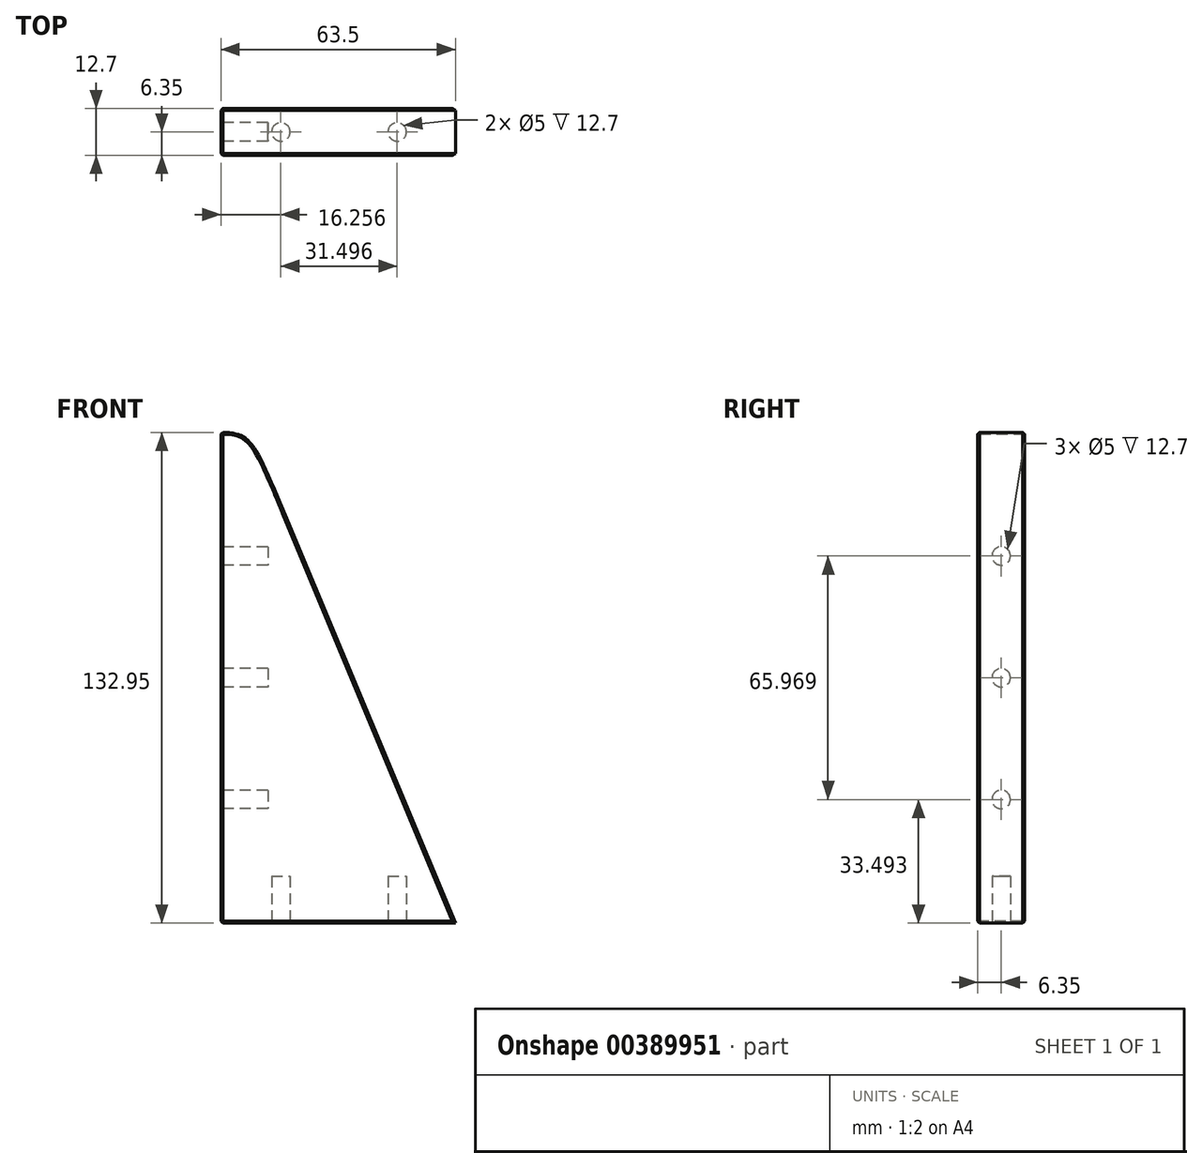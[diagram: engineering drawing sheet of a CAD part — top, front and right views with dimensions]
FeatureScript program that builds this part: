
annotation { "Feature Type Name" : "Feature", "Feature Type Description" : "" }
export const myFeature = defineFeature(function(context is Context, id is Id, definition is map)
    precondition{}
    {
        {
            var Q0;
            Q0=qCreatedBy(makeId("Front.planeOp"),FACE);
            var sketch = newSketch(context, id + "F0", { "sketchPlane" : qUnion([Q0])});
            skLineSegment(sketch, "E0.bottom", {"start": v(63.5, 76.2) * mm, "end": v(-63.5, 76.2) * mm});
            skLineSegment(sketch, "E0.top", {"start": v(63.5, -76.2) * mm, "end": v(-63.5, -76.2) * mm});
            skLineSegment(sketch, "E0.left", {"start": v(63.5, 76.2) * mm, "end": v(63.5, -76.2) * mm});
            skLineSegment(sketch, "E0.right", {"start": v(-63.5, 76.2) * mm, "end": v(-63.5, -76.2) * mm});
            skPoint(sketch, "E0.middle", {"position": v(0, 0) * mm});
            skLineSegment(sketch, "E1", {"start": v(-63.5, 76.2) * mm, "end": v(0, -76.2) * mm});
            skPoint(sketch, "E2.0.internal.orphan", {"position": v(-31.75, 0) * mm});
            skFitSpline(sketch, "E3", {"points": [v(-46.03, 34.28) * mm, v(-63.5, 56.77) * mm], "startDerivative": vector(-25.7, 61.7) * mm, "endDerivative": vector(-24.54, 0.6) * mm});
            skSolve(sketch);
        }
        {
            var Q0;
            {var subQ5=sQuery(id+"F0.wireOp",EDGE,"E3");Q0=makeQuery(id+"F0.imprint","IMPRINT",FACE,{"disambiguationData":[TD([[makeQuery(id+"F0.imprint","IMPRINT",EDGE,{"derivedFrom":subQ5}),1.0]])]});}
            extrude(context, id + "F1", {"entities" : qUnion([Q0]), "depth" : 12.7 * mm});
        }
        {
            var Q0;
            Q0=makeQuery(id+"F1.opExtrude","SWEPT_FACE",FACE,{"disambiguationData":[OSD([sQuery(id+"F0.wireOp",EDGE,"E3")])]});
            var Q1;
            Q1=makeQuery(id+"F1.opExtrude","CAP_FACE",FACE,{"disambiguationData":[OSD([sQuery(id+"F0.wireOp",EDGE,"E0.top"),sQuery(id+"F0.wireOp",EDGE,"E0.right"),sQuery(id+"F0.wireOp",EDGE,"E1"),sQuery(id+"F0.wireOp",EDGE,"E3")])],"isStart":false});
            var Q2;
            Q2=makeQuery(id+"F1.opExtrude","CAP_FACE",FACE,{"disambiguationData":[OSD([sQuery(id+"F0.wireOp",EDGE,"E0.top"),sQuery(id+"F0.wireOp",EDGE,"E0.right"),sQuery(id+"F0.wireOp",EDGE,"E1"),sQuery(id+"F0.wireOp",EDGE,"E3")])],"isStart":true});
            var Q3;
            Q3=makeQuery(id+"F1.opExtrude","SWEPT_FACE",FACE,{"disambiguationData":[OSD([sQuery(id+"F0.wireOp",EDGE,"E0.right")])]});
            chamfer(context, id + "F2", {"entities" : qUnion([Q0, Q1, Q2, Q3]), "width" : 0.5 * mm, "tangentPropagation" : true});
        }
        {
            var Q0;
            Q0=makeQuery(id+"F1.opExtrude","SWEPT_FACE",FACE,{"disambiguationData":[OSD([sQuery(id+"F0.wireOp",EDGE,"E0.right")])]});
            var sketch = newSketch(context, id + "F3", { "sketchPlane" : qUnion([Q0])});
            skLineSegment(sketch, "E4", {"start": v(6.35, 56.25) * mm, "end": v(6.35, -75.7) * mm, "construction": true});
            skLineSegment(sketch, "E5", {"start": v(0.5, -9.72) * mm, "end": v(12.2, -9.72) * mm, "construction": true});
            skLineSegment(sketch, "E6", {"start": v(0.5, 56.25) * mm, "end": v(12.2, -9.72) * mm, "construction": true});
            skLineSegment(sketch, "E7", {"start": v(12.2, 56.25) * mm, "end": v(0.5, -9.72) * mm, "construction": true});
            skLineSegment(sketch, "E8", {"start": v(0.5, -9.72) * mm, "end": v(12.2, -75.7) * mm, "construction": true});
            skLineSegment(sketch, "E9", {"start": v(12.2, -75.7) * mm, "end": v(12.2, -9.72) * mm, "construction": true});
            skLineSegment(sketch, "E10", {"start": v(0.5, -75.7) * mm, "end": v(12.2, -9.72) * mm, "construction": true});
            skCircle(sketch, "E11", {"center": v(6.35, 23.26) * mm, "radius": 2.5 * mm});
            skCircle(sketch, "E12", {"center": v(6.35, -9.72) * mm, "radius": 2.5 * mm});
            skCircle(sketch, "E13", {"center": v(6.35, -42.7) * mm, "radius": 2.5 * mm});
            skSolve(sketch);
        }
        {
            var Q0;
            Q0=makeQuery(id+"F1.opExtrude","SWEPT_FACE",FACE,{"disambiguationData":[OSD([sQuery(id+"F0.wireOp",EDGE,"E0.top")])]});
            var sketch = newSketch(context, id + "F4", { "sketchPlane" : qUnion([Q0])});
            skLineSegment(sketch, "E14", {"start": v(-63, 6.35) * mm, "end": v(0, 6.35) * mm, "construction": true});
            skLineSegment(sketch, "E15", {"start": v(-31.5, 12.2) * mm, "end": v(-31.5, 0.5) * mm, "construction": true});
            skLineSegment(sketch, "E16", {"start": v(-63, 12.2) * mm, "end": v(-31.5, 0.5) * mm, "construction": true});
            skLineSegment(sketch, "E17", {"start": v(-31.5, 12.2) * mm, "end": v(-63, 0.5) * mm, "construction": true});
            skLineSegment(sketch, "E18", {"start": v(-31.5, 12.2) * mm, "end": v(0, 0.5) * mm, "construction": true});
            skLineSegment(sketch, "E19", {"start": v(0, 12.2) * mm, "end": v(-31.5, 0.5) * mm, "construction": true});
            skCircle(sketch, "E20", {"center": v(-47.24, 6.35) * mm, "radius": 2.5 * mm});
            skCircle(sketch, "E21", {"center": v(-15.75, 6.35) * mm, "radius": 2.5 * mm});
            skSolve(sketch);
        }
        {
            var Q0;
            Q0=makeQuery(id+"F4.imprint","IMPRINT",FACE,{"disambiguationData":[TD([[makeQuery(id+"F4.imprint","IMPRINT",EDGE,{"derivedFrom":sQuery(id+"F4.wireOp",EDGE,"E21")}),1.0]])]});
            var Q1;
            Q1=makeQuery(id+"F4.imprint","IMPRINT",FACE,{"disambiguationData":[TD([[makeQuery(id+"F4.imprint","IMPRINT",EDGE,{"derivedFrom":sQuery(id+"F4.wireOp",EDGE,"E20")}),1.0]])]});
            extrude(context, id + "F5", {"entities" : qUnion([Q0, Q1]), "operationType" : NewBodyOperationType.REMOVE, "oppositeDirection" : true, "depth" : 12.7 * mm});
        }
        {
            var Q0;
            Q0=makeQuery(id+"F3.imprint","IMPRINT",FACE,{"disambiguationData":[TD([[makeQuery(id+"F3.imprint","IMPRINT",EDGE,{"derivedFrom":sQuery(id+"F3.wireOp",EDGE,"E13")}),1.0]])]});
            var Q1;
            Q1=makeQuery(id+"F3.imprint","IMPRINT",FACE,{"disambiguationData":[TD([[makeQuery(id+"F3.imprint","IMPRINT",EDGE,{"derivedFrom":sQuery(id+"F3.wireOp",EDGE,"E12")}),1.0]])]});
            var Q2;
            Q2=makeQuery(id+"F3.imprint","IMPRINT",FACE,{"disambiguationData":[TD([[makeQuery(id+"F3.imprint","IMPRINT",EDGE,{"derivedFrom":sQuery(id+"F3.wireOp",EDGE,"E11")}),1.0]])]});
            extrude(context, id + "F6", {"entities" : qUnion([Q0, Q1, Q2]), "operationType" : NewBodyOperationType.REMOVE, "oppositeDirection" : true, "depth" : 12.7 * mm});
        }
    });
